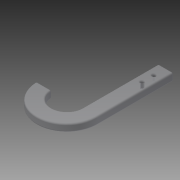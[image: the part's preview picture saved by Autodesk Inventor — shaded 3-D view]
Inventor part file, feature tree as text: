
AUTODESK INVENTOR PART (.ipt)
format: ipt  version: 2014 SP1 (Build 180222100, 222)  size: 150,528 bytes
history: native  units: in
note: dims shown in document units (in); Inventor stores cm internally (conversion verified against a paired STEP export)
features: extrude x2, sketch x2, fillet x1
ambient origin geometry x8: Origin, YZ Plane, XZ Plane, XY Plane, X Axis, Y Axis, Z Axis, Center Point
bodies: Solid1 (feature_tree)
feature tree (5):
  extrude  "Extrusion1"  Depth=5.0in
  extrude  "Extrusion2"  Depth=1.0in
  fillet  "Fillet2"  Radius=0.175in
  sketch  "Sketch1"  dims[d0=1.0in d1=5.0in]
  sketch  "Sketch2"  dims[d2=0.5in d3=0.0in d4=1.0in d6=0.175in d7=0.7874in d9=0.7654in d10=0.3937in d12=1.0in d14=0.5in d15=0.0in d16=0.1in]
